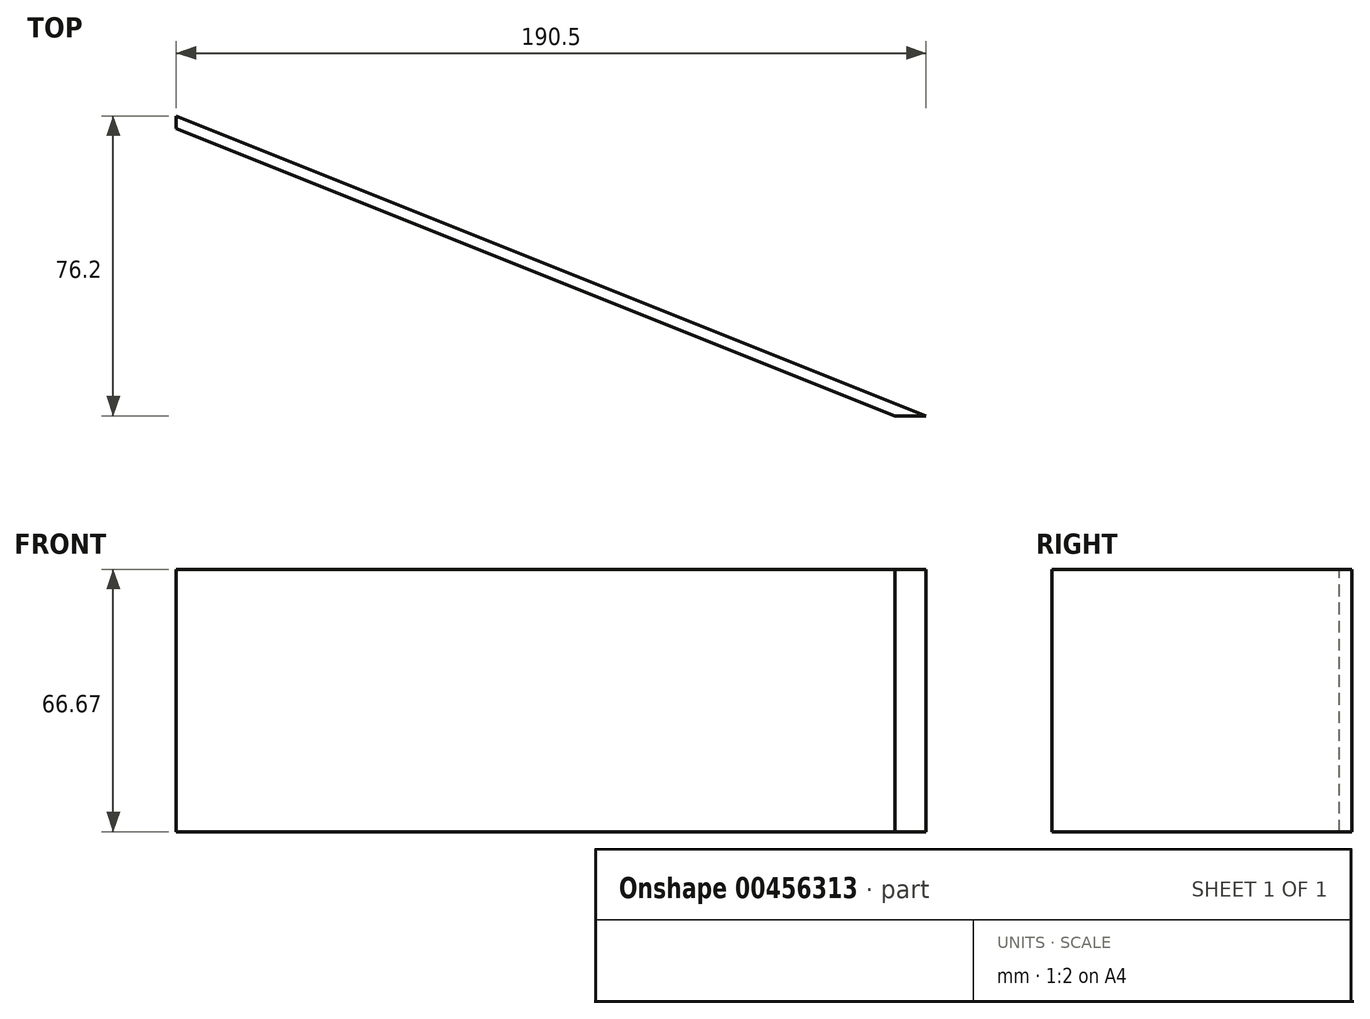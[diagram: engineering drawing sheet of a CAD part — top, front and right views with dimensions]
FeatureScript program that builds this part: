
annotation { "Feature Type Name" : "Feature", "Feature Type Description" : "" }
export const myFeature = defineFeature(function(context is Context, id is Id, definition is map)
    precondition{}
    {
        {
            var Q0;
            Q0=qCreatedBy(makeId("Top.planeOp"),FACE);
            var sketch = newSketch(context, id + "F0", { "sketchPlane" : qUnion([Q0])});
            skLineSegment(sketch, "E0.bottom", {"start": v(0, 0) * mm, "end": v(190.5, 0) * mm});
            skLineSegment(sketch, "E0.top", {"start": v(0, 76.2) * mm, "end": v(190.5, 76.2) * mm});
            skLineSegment(sketch, "E0.left", {"start": v(0, 0) * mm, "end": v(0, 76.2) * mm});
            skLineSegment(sketch, "E0.right", {"start": v(190.5, 0) * mm, "end": v(190.5, 76.2) * mm});
            skSolve(sketch);
        }
        {
            var Q0;
            Q0=makeQuery(id+"F0.imprint","IMPRINT",FACE,{"disambiguationData":[TD([[makeQuery(id+"F0.imprint","IMPRINT",EDGE,{"derivedFrom":sQuery(id+"F0.wireOp",EDGE,"E0.bottom")}),1.0]])]});
            extrude(context, id + "F1", {"entities" : qUnion([Q0]), "depth" : 66.67 * mm});
        }
        {
            var Q0;
            Q0=makeQuery(id+"F1.opExtrude","CAP_FACE",FACE,{"disambiguationData":[OSD([sQuery(id+"F0.wireOp",EDGE,"E0.bottom"),sQuery(id+"F0.wireOp",EDGE,"E0.top"),sQuery(id+"F0.wireOp",EDGE,"E0.left"),sQuery(id+"F0.wireOp",EDGE,"E0.right")])],"isStart":false});
            var sketch = newSketch(context, id + "F2", { "sketchPlane" : qUnion([Q0])});
            skLineSegment(sketch, "E1", {"start": v(190.5, 0) * mm, "end": v(0, 76.2) * mm});
            skSolve(sketch);
        }
        {
            var Q0;
            Q0=makeQuery(id+"F2.imprint","IMPRINT",FACE,{"disambiguationData":[TD([[makeQuery(id+"F2.imprint","IMPRINT",EDGE,{"derivedFrom":sQuery(id+"F2.wireOp",EDGE,"E1")}),-1.0]])]});
            extrude(context, id + "F3", {"entities" : qUnion([Q0]), "operationType" : NewBodyOperationType.REMOVE, "oppositeDirection" : true, "depth" : 76.2 * mm});
        }
        {
            var Q0;
            Q0=makeQuery(id+"F1.opExtrude","CAP_FACE",FACE,{"disambiguationData":[OSD([sQuery(id+"F0.wireOp",EDGE,"E0.bottom"),sQuery(id+"F0.wireOp",EDGE,"E0.top"),sQuery(id+"F0.wireOp",EDGE,"E0.left"),sQuery(id+"F0.wireOp",EDGE,"E0.right")])],"isStart":false});
            var sketch = newSketch(context, id + "F4", { "sketchPlane" : qUnion([Q0])});
            skLineSegment(sketch, "E2", {"start": v(0, 76.2) * mm, "end": v(0, 73.03) * mm});
            skLineSegment(sketch, "E3", {"start": v(0, 76.2) * mm, "end": v(190.5, 0) * mm});
            skLineSegment(sketch, "E4", {"start": v(0, 73.03) * mm, "end": v(182.56, 0) * mm});
            skSolve(sketch);
        }
        {
            var Q0;
            {var subQ0=sQuery(id+"F4.wireOp",EDGE,"E4");Q0=makeQuery(id+"F4.imprint","IMPRINT",FACE,{"disambiguationData":[TD([[makeQuery(id+"F4.imprint","IMPRINT",EDGE,{"derivedFrom":subQ0}),-1.0]])]});}
            extrude(context, id + "F5", {"entities" : qUnion([Q0]), "operationType" : NewBodyOperationType.REMOVE, "oppositeDirection" : true, "depth" : 76.2 * mm});
        }
    });
